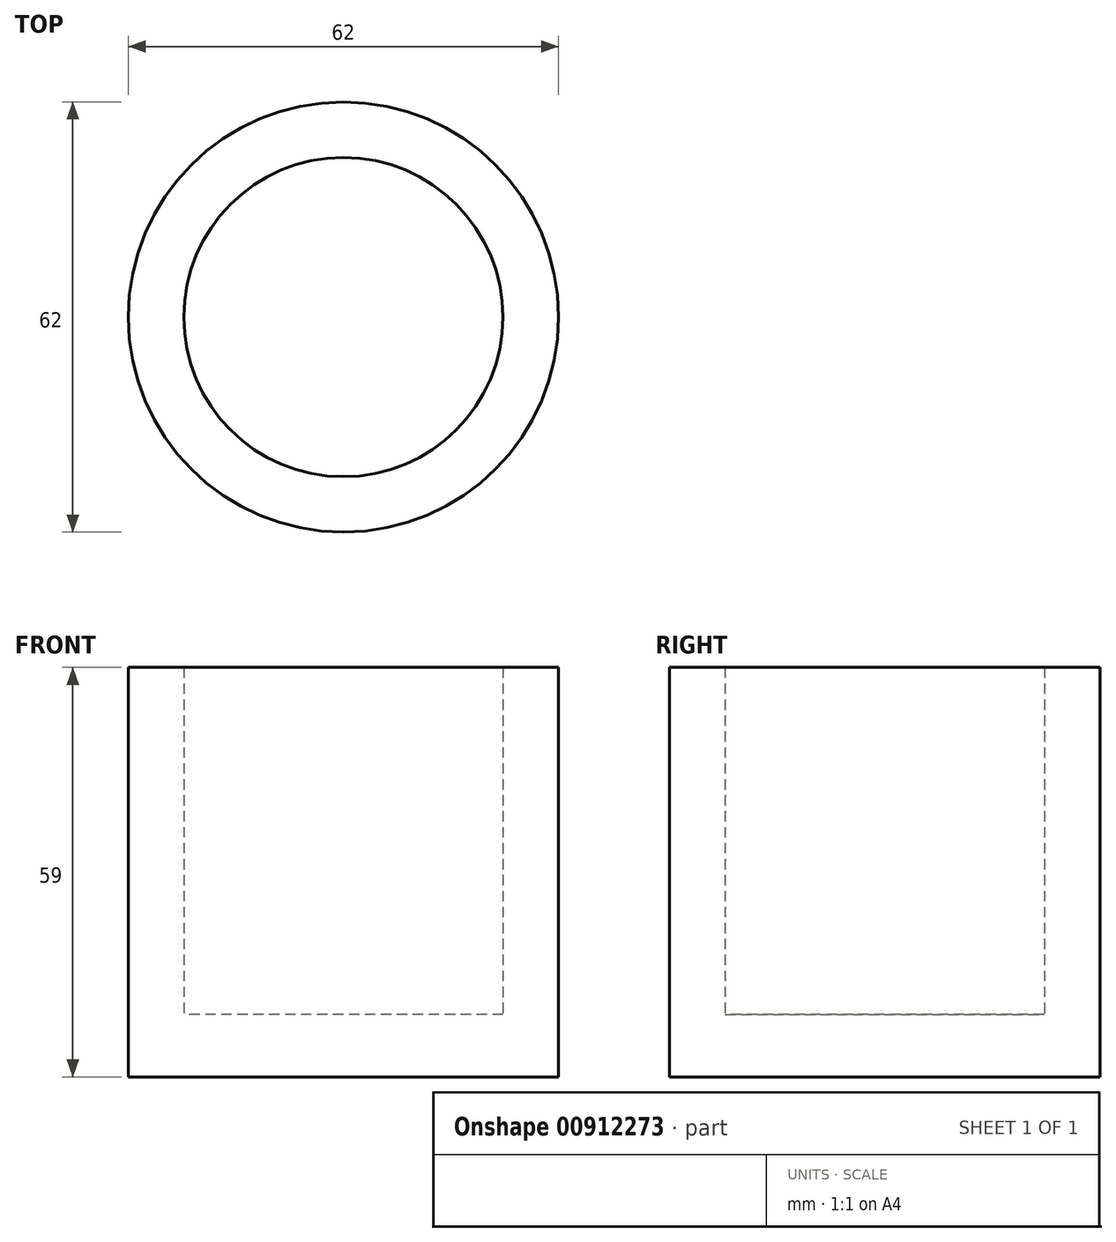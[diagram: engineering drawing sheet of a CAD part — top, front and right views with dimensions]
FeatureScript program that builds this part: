
annotation { "Feature Type Name" : "Feature", "Feature Type Description" : "" }
export const myFeature = defineFeature(function(context is Context, id is Id, definition is map)
    precondition{}
    {
        {
            var Q0;
            Q0=qCreatedBy(makeId("Top.planeOp"),FACE);
            var sketch = newSketch(context, id + "F0", { "sketchPlane" : qUnion([Q0])});
            skCircle(sketch, "E0", {"center": v(0, 0) * mm, "radius": 31 * mm});
            skLineSegment(sketch, "E1", {"start": v(0, 0) * mm, "end": v(31, 0) * mm, "construction": true});
            skLineSegment(sketch, "E2", {"start": v(31, 0) * mm, "end": v(-31, 0) * mm, "construction": true});
            skPoint(sketch, "E2.endSnap0", {"position": v(15.5, 0) * mm});
            skCircle(sketch, "E3", {"center": v(0, 0) * mm, "radius": 23 * mm});
            skLineSegment(sketch, "E4", {"start": v(0, -23) * mm, "end": v(0, 23) * mm});
            skSolve(sketch);
        }
        {
            var Q0;
            Q0=makeQuery(id+"F0.imprint","IMPRINT",FACE,{"disambiguationData":[TD([[makeQuery(id+"F0.imprint","IMPRINT",EDGE,{"derivedFrom":sQuery(id+"F0.wireOp",EDGE,"E0")}),1.0]])]});
            extrude(context, id + "F1", {"entities" : qUnion([Q0]), "depth" : 59 * mm, "offsetDistance" : 25 * mm});
        }
        {
            var Q0;
            {var subQ0=sQuery(id+"F0.wireOp",EDGE,"E4");Q0=makeQuery(id+"F0.imprint","IMPRINT",FACE,{"disambiguationData":[TD([[makeQuery(id+"F0.imprint","IMPRINT",EDGE,{"derivedFrom":subQ0}),1.0]])]});}
            var Q1;
            {var subQ0=sQuery(id+"F0.wireOp",EDGE,"E4");Q1=makeQuery(id+"F0.imprint","IMPRINT",FACE,{"disambiguationData":[TD([[makeQuery(id+"F0.imprint","IMPRINT",EDGE,{"derivedFrom":subQ0}),-1.0]])]});}
            extrude(context, id + "F2", {"entities" : qUnion([Q0, Q1]), "operationType" : NewBodyOperationType.ADD, "depth" : 9 * mm, "offsetDistance" : 25 * mm});
        }
    });
